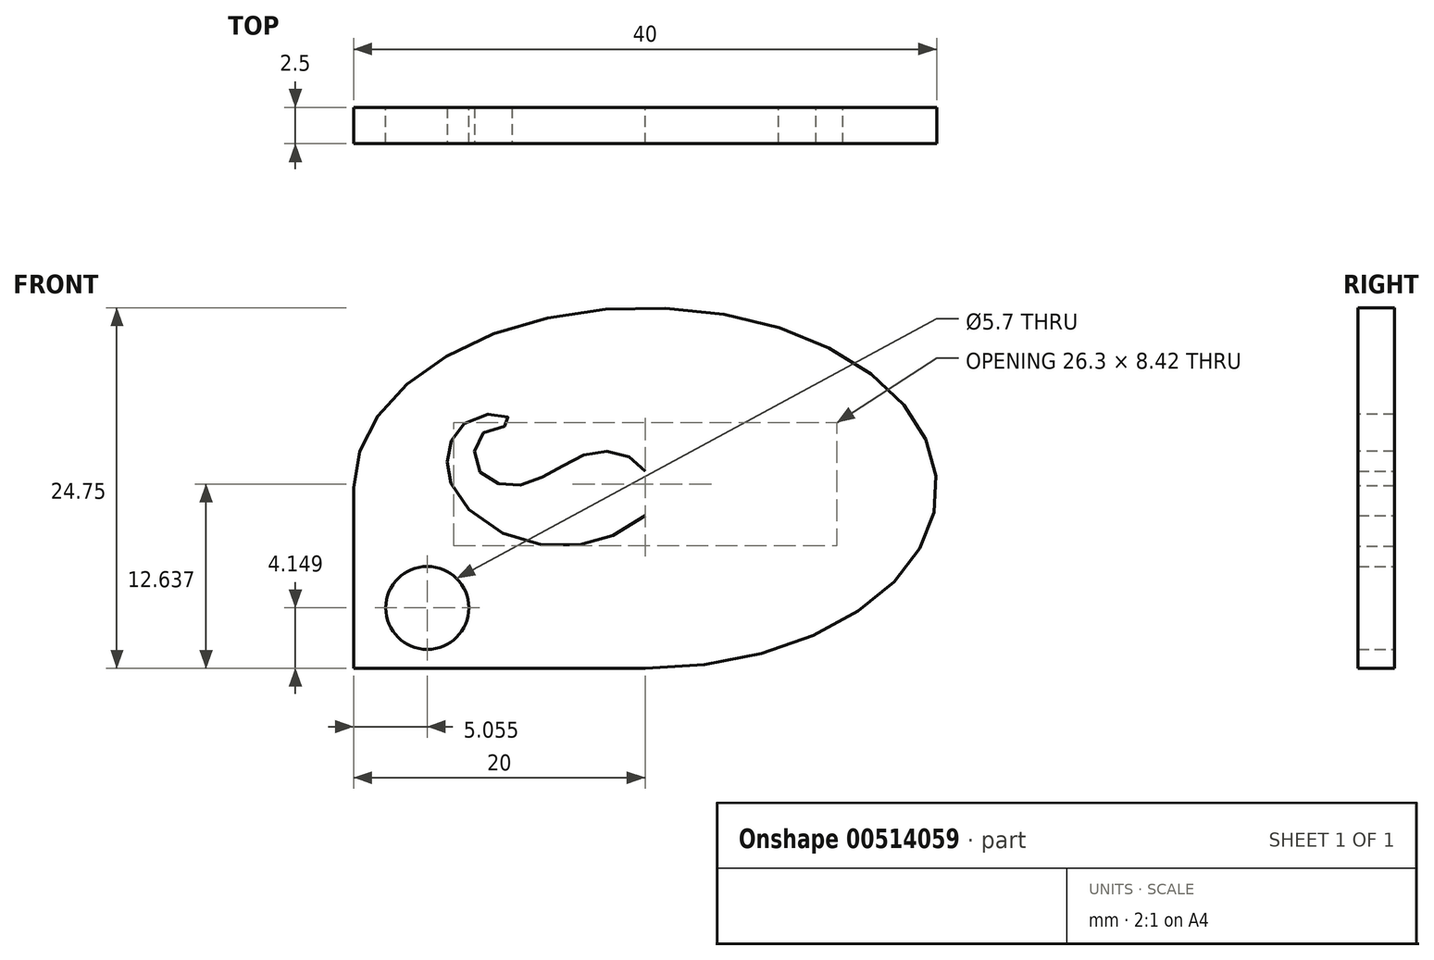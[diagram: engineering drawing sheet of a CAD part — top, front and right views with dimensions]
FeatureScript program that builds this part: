
annotation { "Feature Type Name" : "Feature", "Feature Type Description" : "" }
export const myFeature = defineFeature(function(context is Context, id is Id, definition is map)
    precondition{}
    {
        {
            var Q0;
            Q0=qCreatedBy(makeId("Front.planeOp"),FACE);
            var sketch = newSketch(context, id + "F0", { "sketchPlane" : qUnion([Q0])});
            skLineSegment(sketch, "E0.top", {"start": v(-16, 3.43) * mm, "end": v(-36, 3.43) * mm});
            skLineSegment(sketch, "E0.right", {"start": v(-36, 16) * mm, "end": v(-36, 3.43) * mm});
            skPoint(sketch, "E0.middle", {"position": v(-16, 16) * mm});
            skEllipticalArc(sketch, "E1", {});
            skPoint(sketch, "E2.orphan", {"position": v(-36, 28.57) * mm});
            skPoint(sketch, "E3.orphan", {"position": v(4, 28.57) * mm});
            skPoint(sketch, "E4.orphan", {"position": v(4, 3.43) * mm});
            skPoint(sketch, "E5.0.internal.orphan", {"position": v(-16, 16.97) * mm});
            skPoint(sketch, "E5.9.internal.orphan", {"position": v(-7.9, 16) * mm});
            skLineSegment(sketch, "E6", {"start": v(-16, 16.97) * mm, "end": v(-16, 13.9) * mm});
            skFitSpline(sketch, "E7", {"points": [v(-16, 16.97) * mm, v(-15.68, 17.35) * mm, v(-15.25, 17.73) * mm, v(-14.8, 17.98) * mm, v(-14.3, 18.18) * mm, v(-13.7, 18.3) * mm, v(-12.97, 18.34) * mm, v(-12.35, 18.26) * mm, v(-11.8, 18.09) * mm, v(-11.27, 17.85) * mm, v(-10.72, 17.54) * mm, v(-10.2, 17.23) * mm, v(-9.7, 16.97) * mm, v(-9, 16.57) * mm, v(-8.36, 16.29) * mm, v(-7.8, 16.1) * mm, v(-7.35, 16) * mm, v(-6.8, 15.93) * mm, v(-6.22, 16) * mm, v(-5.69, 16.22) * mm, v(-5.23, 16.45) * mm, v(-4.78, 16.8) * mm, v(-4.5, 17.23) * mm, v(-4.35, 17.76) * mm, v(-4.3, 18.3) * mm, v(-4.38, 18.74) * mm, v(-4.57, 19.13) * mm, v(-4.92, 19.6) * mm, v(-5.35, 19.87) * mm, v(-5.97, 20.03) * mm, v(-6.5, 20.06) * mm, v(-6.8, 20.18) * mm, v(-6.85, 20.43) * mm, v(-6.7, 20.62) * mm, v(-6.38, 20.72) * mm, v(-5.95, 20.81) * mm, v(-5.51, 20.87) * mm, v(-4.85, 20.81) * mm, v(-4.11, 20.53) * mm, v(-3.51, 20.18) * mm, v(-3.08, 19.75) * mm, v(-2.82, 19.35) * mm, v(-2.61, 18.84) * mm, v(-2.48, 18.4) * mm, v(-2.44, 17.84) * mm, v(-2.44, 17.26) * mm, v(-2.48, 16.78) * mm, v(-2.64, 16.23) * mm, v(-2.94, 15.59) * mm, v(-3.78, 14.45) * mm, v(-5.37, 13.19) * mm, v(-6.91, 12.44) * mm, v(-8.8, 11.92) * mm, v(-10.52, 11.8) * mm, v(-12, 12.01) * mm, v(-13.2, 12.35) * mm, v(-14.62, 12.95) * mm, v(-16, 13.9) * mm], "startDerivative": vector(20, 25.47) * mm, "endDerivative": vector(-48.58, 37.24) * mm});
            skPoint(sketch, "E8.MirrorP", {"position": v(-24.1, 16) * mm});
            skFitSpline(sketch, "E9.MirrorCS", {"points": [v(-16, 16.97) * mm, v(-16.32, 17.35) * mm, v(-16.75, 17.73) * mm, v(-17.2, 17.98) * mm, v(-17.7, 18.18) * mm, v(-18.3, 18.3) * mm, v(-19.03, 18.34) * mm, v(-19.65, 18.26) * mm, v(-20.2, 18.09) * mm, v(-20.73, 17.85) * mm, v(-21.28, 17.54) * mm, v(-21.8, 17.23) * mm, v(-22.3, 16.97) * mm, v(-23, 16.57) * mm, v(-23.64, 16.29) * mm, v(-24.2, 16.1) * mm, v(-24.65, 16) * mm, v(-25.2, 15.93) * mm, v(-25.78, 16) * mm, v(-26.31, 16.22) * mm, v(-26.77, 16.45) * mm, v(-27.22, 16.8) * mm, v(-27.5, 17.23) * mm, v(-27.65, 17.76) * mm, v(-27.7, 18.3) * mm, v(-27.62, 18.74) * mm, v(-27.43, 19.13) * mm, v(-27.08, 19.6) * mm, v(-26.65, 19.87) * mm, v(-26.03, 20.03) * mm, v(-25.5, 20.06) * mm, v(-25.2, 20.18) * mm, v(-25.15, 20.43) * mm, v(-25.3, 20.62) * mm, v(-25.62, 20.72) * mm, v(-26.05, 20.81) * mm, v(-26.49, 20.87) * mm, v(-27.15, 20.81) * mm, v(-27.89, 20.53) * mm, v(-28.49, 20.18) * mm, v(-28.92, 19.75) * mm, v(-29.18, 19.35) * mm, v(-29.39, 18.84) * mm, v(-29.52, 18.4) * mm, v(-29.56, 17.84) * mm, v(-29.56, 17.26) * mm, v(-29.52, 16.78) * mm, v(-29.36, 16.23) * mm, v(-29.06, 15.59) * mm, v(-28.22, 14.45) * mm, v(-26.63, 13.19) * mm, v(-25.09, 12.44) * mm, v(-23.2, 11.92) * mm, v(-21.48, 11.8) * mm, v(-20, 12.01) * mm, v(-18.8, 12.35) * mm, v(-17.38, 12.95) * mm, v(-16, 13.9) * mm], "startDerivative": vector(-20, 25.47) * mm, "endDerivative": vector(48.58, 37.24) * mm});
            skCircle(sketch, "E10", {"center": v(-30.95, 7.58) * mm, "radius": 2.85 * mm});
            const initialGuessF0  = {"E1": [-0.015999998897314068, 0.01580262410055137, 1, 0, 0.02, 0.012374585767895326, 4.71238898038469, 3.141592653589793]};
            skSetInitialGuess(sketch, initialGuessF0);
            skSolve(sketch);
        }
        {
            var Q0;
            {var subQ2=sQuery(id+"F0.wireOp",EDGE,"E0.top");Q0=makeQuery(id+"F0.imprint","IMPRINT",FACE,{"disambiguationData":[TD([[makeQuery(id+"F0.imprint","IMPRINT",EDGE,{"derivedFrom":subQ2}),-1.0]])]});}
            extrude(context, id + "F1", {"entities" : qUnion([Q0]), "depth" : 2.5 * mm});
        }
    });
